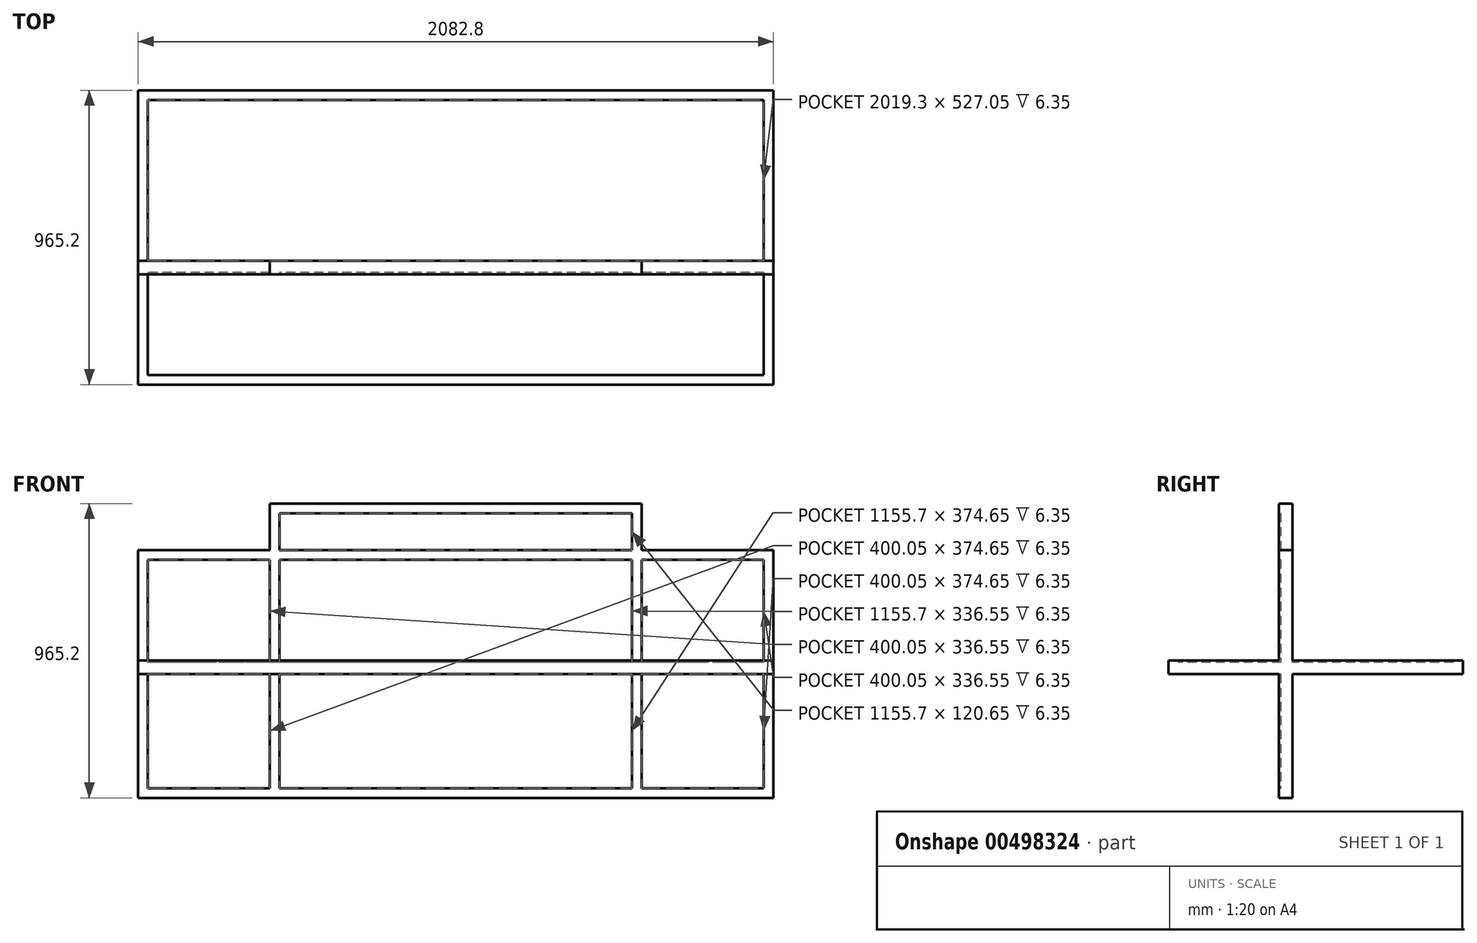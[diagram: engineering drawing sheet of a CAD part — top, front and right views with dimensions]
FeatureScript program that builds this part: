
annotation { "Feature Type Name" : "Feature", "Feature Type Description" : "" }
export const myFeature = defineFeature(function(context is Context, id is Id, definition is map)
    precondition{}
    {
        {
            var Q0;
            Q0=qCreatedBy(makeId("Front.planeOp"),FACE);
            var sketch = newSketch(context, id + "F0", { "sketchPlane" : qUnion([Q0])});
            skLineSegment(sketch, "E0.bottom", {"start": v(1016, 381) * mm, "end": v(-1016, 381) * mm});
            skLineSegment(sketch, "E0.top", {"start": v(1016, -381) * mm, "end": v(-1016, -381) * mm});
            skLineSegment(sketch, "E0.left", {"start": v(1016, 381) * mm, "end": v(1016, -381) * mm});
            skLineSegment(sketch, "E0.right", {"start": v(-1016, 381) * mm, "end": v(-1016, -381) * mm});
            skPoint(sketch, "E0.middle", {"position": v(0, 0) * mm});
            skLineSegment(sketch, "E1.0", {"start": v(1041.4, 406.4) * mm, "end": v(-1041.4, 406.4) * mm});
            skLineSegment(sketch, "E1.1", {"start": v(1041.4, 406.4) * mm, "end": v(1041.4, -406.4) * mm});
            skLineSegment(sketch, "E1.2", {"start": v(1041.4, -406.4) * mm, "end": v(-1041.4, -406.4) * mm});
            skLineSegment(sketch, "E1.3", {"start": v(-1041.4, 406.4) * mm, "end": v(-1041.4, -406.4) * mm});
            skLineSegment(sketch, "E2.bottom", {"start": v(1009.65, 374.65) * mm, "end": v(-1009.65, 374.65) * mm});
            skLineSegment(sketch, "E2.top", {"start": v(1009.65, -374.65) * mm, "end": v(-1009.65, -374.65) * mm});
            skLineSegment(sketch, "E2.left", {"start": v(1009.65, 374.65) * mm, "end": v(1009.65, -374.65) * mm});
            skLineSegment(sketch, "E2.right", {"start": v(-1009.65, 374.65) * mm, "end": v(-1009.65, -374.65) * mm});
            skSolve(sketch);
        }
        {
            var Q0;
            Q0 = qSketchRegion(id + "F0", true);
            extrude(context, id + "F1", {"entities" : qUnion([Q0]), "depth" : 44.45 * mm});
        }
        {
            var Q0;
            Q0=makeQuery(id+"F0.imprint","IMPRINT",FACE,{"disambiguationData":[TD([[makeQuery(id+"F0.imprint","IMPRINT",EDGE,{"derivedFrom":sQuery(id+"F0.wireOp",EDGE,"E0.bottom")}),1.0]])]});
            var Q1;
            Q1=makeQuery(id+"F0.imprint","IMPRINT",FACE,{"disambiguationData":[TD([[makeQuery(id+"F0.imprint","IMPRINT",EDGE,{"derivedFrom":sQuery(id+"F0.wireOp",EDGE,"E2.bottom")}),1.0]])]});
            extrude(context, id + "F2", {"entities" : qUnion([Q0, Q1]), "depth" : 38.1 * mm});
        }
        {
            var Q0;
            Q0=makeQuery(id+"F0.imprint","IMPRINT",FACE,{"disambiguationData":[TD([[makeQuery(id+"F0.imprint","IMPRINT",EDGE,{"derivedFrom":sQuery(id+"F0.wireOp",EDGE,"E0.bottom")}),1.0]])]});
            extrude(context, id + "F3", {"entities" : qUnion([Q0]), "operationType" : NewBodyOperationType.ADD, "depth" : 44.45 * mm, "hasSecondDirection" : true, "secondDirectionOppositeDirection" : false, "secondDirectionDepth" : 38.1 * mm});
        }
        {
            var Q0;
            Q0=qCreatedBy(makeId("Front.planeOp"),FACE);
            var sketch = newSketch(context, id + "F4", { "sketchPlane" : qUnion([Q0])});
            skLineSegment(sketch, "E3.bottom", {"start": v(584.2, 533.4) * mm, "end": v(-584.2, 533.4) * mm});
            skLineSegment(sketch, "E3.top", {"start": v(584.2, -381) * mm, "end": v(-584.2, -381) * mm});
            skLineSegment(sketch, "E3.left", {"start": v(584.2, 533.4) * mm, "end": v(584.2, -381) * mm});
            skLineSegment(sketch, "E3.right", {"start": v(-584.2, 533.4) * mm, "end": v(-584.2, -381) * mm});
            skPoint(sketch, "E3.middle", {"position": v(0, 76.2) * mm});
            skLineSegment(sketch, "E4.0", {"start": v(609.6, 558.8) * mm, "end": v(-609.6, 558.8) * mm});
            skLineSegment(sketch, "E4.1", {"start": v(609.6, 558.8) * mm, "end": v(609.6, -406.4) * mm});
            skLineSegment(sketch, "E4.2", {"start": v(609.6, -406.4) * mm, "end": v(-609.6, -406.4) * mm});
            skLineSegment(sketch, "E4.3", {"start": v(-609.6, 558.8) * mm, "end": v(-609.6, -406.4) * mm});
            skLineSegment(sketch, "E5.bottom", {"start": v(577.85, 527.05) * mm, "end": v(-577.85, 527.05) * mm});
            skLineSegment(sketch, "E5.top", {"start": v(577.85, -374.65) * mm, "end": v(-577.85, -374.65) * mm});
            skLineSegment(sketch, "E5.left", {"start": v(577.85, 527.05) * mm, "end": v(577.85, -374.65) * mm});
            skLineSegment(sketch, "E5.right", {"start": v(-577.85, 527.05) * mm, "end": v(-577.85, -374.65) * mm});
            skSolve(sketch);
        }
        {
            var Q0;
            Q0=makeQuery(id+"F4.imprint","IMPRINT",FACE,{"disambiguationData":[TD([[makeQuery(id+"F4.imprint","IMPRINT",EDGE,{"derivedFrom":sQuery(id+"F4.wireOp",EDGE,"E5.bottom")}),1.0]])]});
            var Q1;
            Q1=makeQuery(id+"F4.imprint","IMPRINT",FACE,{"disambiguationData":[TD([[makeQuery(id+"F4.imprint","IMPRINT",EDGE,{"derivedFrom":sQuery(id+"F4.wireOp",EDGE,"E3.bottom")}),1.0]])]});
            extrude(context, id + "F5", {"entities" : qUnion([Q0, Q1]), "depth" : 38.1 * mm});
        }
        {
            var Q0;
            Q0=makeQuery(id+"F4.imprint","IMPRINT",FACE,{"disambiguationData":[TD([[makeQuery(id+"F4.imprint","IMPRINT",EDGE,{"derivedFrom":sQuery(id+"F4.wireOp",EDGE,"E3.bottom")}),-1.0]])]});
            extrude(context, id + "F6", {"entities" : qUnion([Q0]), "depth" : 44.45 * mm});
        }
        {
            var Q0;
            Q0=makeQuery(id+"F4.imprint","IMPRINT",FACE,{"disambiguationData":[TD([[makeQuery(id+"F4.imprint","IMPRINT",EDGE,{"derivedFrom":sQuery(id+"F4.wireOp",EDGE,"E3.bottom")}),1.0]])]});
            var Q1;
            Q1=makeQuery(id+"F4.imprint","IMPRINT",FACE,{"disambiguationData":[TD([[makeQuery(id+"F4.imprint","IMPRINT",EDGE,{"derivedFrom":sQuery(id+"F4.wireOp",EDGE,"E3.bottom")}),-1.0]])]});
            extrude(context, id + "F7", {"entities" : qUnion([Q0, Q1]), "operationType" : NewBodyOperationType.ADD, "depth" : 44.45 * mm, "hasSecondDirection" : true, "secondDirectionOppositeDirection" : false, "secondDirectionDepth" : 38.1 * mm});
        }
        {
            var Q0;
            Q0=qCreatedBy(makeId("Top.planeOp"),FACE);
            var sketch = newSketch(context, id + "F8", { "sketchPlane" : qUnion([Q0])});
            skLineSegment(sketch, "E6.bottom", {"start": v(1016, 533.4) * mm, "end": v(-1016, 533.4) * mm});
            skLineSegment(sketch, "E6.top", {"start": v(1016, -381) * mm, "end": v(-1016, -381) * mm});
            skLineSegment(sketch, "E6.left", {"start": v(1016, 533.4) * mm, "end": v(1016, -381) * mm});
            skLineSegment(sketch, "E6.right", {"start": v(-1016, 533.4) * mm, "end": v(-1016, -381) * mm});
            skPoint(sketch, "E6.middle", {"position": v(0, 76.2) * mm});
            skLineSegment(sketch, "E7.0", {"start": v(1041.4, 558.8) * mm, "end": v(-1041.4, 558.8) * mm});
            skLineSegment(sketch, "E7.1", {"start": v(1041.4, 558.8) * mm, "end": v(1041.4, -406.4) * mm});
            skLineSegment(sketch, "E7.2", {"start": v(1041.4, -406.4) * mm, "end": v(-1041.4, -406.4) * mm});
            skLineSegment(sketch, "E7.3", {"start": v(-1041.4, 558.8) * mm, "end": v(-1041.4, -406.4) * mm});
            skLineSegment(sketch, "E8.bottom", {"start": v(1009.65, 527.05) * mm, "end": v(-1009.65, 527.05) * mm});
            skLineSegment(sketch, "E8.top", {"start": v(1009.65, -374.65) * mm, "end": v(-1009.65, -374.65) * mm});
            skLineSegment(sketch, "E8.left", {"start": v(1009.65, 527.05) * mm, "end": v(1009.65, -374.65) * mm});
            skLineSegment(sketch, "E8.right", {"start": v(-1009.65, 527.05) * mm, "end": v(-1009.65, -374.65) * mm});
            skSolve(sketch);
        }
        {
            var Q0;
            Q0=makeQuery(id+"F8.imprint","IMPRINT",FACE,{"disambiguationData":[TD([[makeQuery(id+"F8.imprint","IMPRINT",EDGE,{"derivedFrom":sQuery(id+"F8.wireOp",EDGE,"E8.bottom")}),1.0]])]});
            var Q1;
            Q1=makeQuery(id+"F8.imprint","IMPRINT",FACE,{"disambiguationData":[TD([[makeQuery(id+"F8.imprint","IMPRINT",EDGE,{"derivedFrom":sQuery(id+"F8.wireOp",EDGE,"E6.bottom")}),1.0]])]});
            extrude(context, id + "F9", {"entities" : qUnion([Q0, Q1]), "depth" : 38.1 * mm});
        }
        {
            var Q0;
            Q0=makeQuery(id+"F8.imprint","IMPRINT",FACE,{"disambiguationData":[TD([[makeQuery(id+"F8.imprint","IMPRINT",EDGE,{"derivedFrom":sQuery(id+"F8.wireOp",EDGE,"E6.bottom")}),-1.0]])]});
            var Q1;
            Q1=makeQuery(id+"F8.imprint","IMPRINT",FACE,{"disambiguationData":[TD([[makeQuery(id+"F8.imprint","IMPRINT",EDGE,{"derivedFrom":sQuery(id+"F8.wireOp",EDGE,"E6.bottom")}),1.0]])]});
            extrude(context, id + "F10", {"entities" : qUnion([Q0, Q1]), "depth" : 44.45 * mm, "hasSecondDirection" : true, "secondDirectionOppositeDirection" : false, "secondDirectionDepth" : 38.1 * mm});
        }
        {
            var Q0;
            Q0=makeQuery(id+"F8.imprint","IMPRINT",FACE,{"disambiguationData":[TD([[makeQuery(id+"F8.imprint","IMPRINT",EDGE,{"derivedFrom":sQuery(id+"F8.wireOp",EDGE,"E6.bottom")}),-1.0]])]});
            extrude(context, id + "F11", {"entities" : qUnion([Q0]), "operationType" : NewBodyOperationType.ADD, "depth" : 38.1 * mm});
        }
    });
